# Revit family: pl-erp40160ha3_50hz
name_source: partatom
category: 機械設備
units: mm (PartAtom-declared; Revit-internal decimal feet)

## family parameters
OmniClass タイトル = Split System Air Conditioning Units
OmniClass 番号 = 23.75.10.24.21.27.27
パーツ タイプ = 標準
ロード時にボイドで切り取り = いいえ
丸型コネクタ寸法 = 直径を使用
作業面ベース = いいえ
共有 = いいえ
常に垂直 = はい
部屋計算ポイント = はい

## types (11) — shared parameters
Clearance Back = 1500  [stored 4.92126 ft]
Clearance Bottom = 1800  [stored 5.90551 ft]
Clearance Front = 1500  [stored 4.92126 ft]
Clearance Left = 1500  [stored 4.92126 ft]
Clearance Right = 1500  [stored 4.92126 ft]
Depth = 840  [stored 2.75591 ft]
IfcExportAs = IfcUnitaryEquipmentType
IfcExportType = AIRCONDITIONINGUNIT
OmniClassCode = 23-33 17 13 11
Panel Depth = 950  [stored 3.1168 ft]
Panel Height = 35  [stored 0.114829 ft]
Panel Width = 950  [stored 3.1168 ft]
URL = https://www.mitsubishielectric.co.jp
Uniclass2015Code = Pr_70_65_03_84
Uniclass2015Title = Split coil remote air cooled condensing units
Uniclass2015Version = Systems v1.9
Width = 840  [stored 2.75591 ft]
ケーブルサイズ = 0 mm
サービススペース = はい
ドレン管径 = 25 mm
ドレン管径(外径) = 32 mm
ドレン管高さ = 190
パネルマテリアル = <カテゴリ別>
仕様書バージョン = Version1.0
企業コード = 108420
冷媒ガス管高さ = 170  [stored 0.557743 ft]
冷媒液管高さ = 140  [stored 0.459318 ft]
冷媒管径 = 100 mm
分類コード = 5.0053E+13
参照している仕様書等のバージョン = 公共建築物標準仕様書（機械設備工事編）平成31年度版
吊りボルト_H = 105  [stored 0.344488 ft]
吊り位置X = 795  [stored 2.60827 ft]
吊り位置Y = 660
周波数 = 50 Hz
呼称 = 室内機_カセット形 (4方向吹出形)
始動方式 = 直入
形式 = カセット形 (4方向吹出形)
推奨ブレーカー容量 = 0 A
本体マテリアル = <カテゴリ別>
極数 = 1
法定耐用年数 = 6
消費電力 = 0 kW
消費電力_冷房 = 0 kW
消費電力_暖房 = 0 kW
発停方法 = 付属スイッチ
相 = 1
積算_科目 = 1 空気調和設備
符号 = PAC_CK4
製品出荷対象 = 国内
製品質量_パネル = 4.50 kg
製造元 = 三菱電機株式会社
設置方法 = カセット形
説明 = 店舗・事務所用パッケージエアコン(Mr.SLIM) 4方向天井カセット形
負荷分類 = 3_ファン類
運転質量 = 0.00 kg
電動機出力_送風機 = 0 kW
電圧 = 0 V
電源_H = 37
zero-valued in all types: 価格, 有効加湿量

## per-type parameters (varying)
- 天井4方向_PL-ERP40HA3: Clearance Top=265  [stored 0.869423 ft]; Height=258  [stored 0.846457 ft]; MAX風量=960.0 m³/h; MID風量=720.0 m³/h; MID風量2=660.0 m³/h; MIN風量=600.0 m³/h; 冷媒ガス管径=12.7 mm; 冷媒ガス管長さ=76.5  [stored 0.250984 ft]; 冷媒液管径=6.35 mm; 冷媒液管長さ=72.5  [stored 0.237861 ft]; 冷媒管径符号=Ac; 冷房能力=4 kW; 暖房能力=4 kW; 構成品番=PL-ERP40HA3; 製品質量=24.50 kg; 製品質量_本体=20.00 kg; 質量=29.40 kg; 音響パワーレベル(dB)=45; 音響パワーレベル_中 (dB)=44; 音響パワーレベル_弱 (dB)=43; 音響パワーレベル_強 (dB)=45; 音響パワーレベル_静 (dB)=42; 風量=960.0 m³/h; 風量_中 (㎥/min)=12; 風量_弱 (㎥/min)=11; 風量_強 (㎥/min)=16; 風量_静 (㎥/min)=10
- 天井4方向_PL-ERP45HA3: Clearance Top=265  [stored 0.869423 ft]; Height=258  [stored 0.846457 ft]; MAX風量=960.0 m³/h; MID風量=720.0 m³/h; MID風量2=660.0 m³/h; MIN風量=600.0 m³/h; 冷媒ガス管径=12.7 mm; 冷媒ガス管長さ=76.5  [stored 0.250984 ft]; 冷媒液管径=6.35 mm; 冷媒液管長さ=72.5  [stored 0.237861 ft]; 冷媒管径符号=Ac; 冷房能力=4 kW; 暖房能力=5 kW; 構成品番=PL-ERP45HA3; 製品質量=24.50 kg; 製品質量_本体=20.00 kg; 質量=29.40 kg; 音響パワーレベル(dB)=46; 音響パワーレベル_中 (dB)=44; 音響パワーレベル_弱 (dB)=43; 音響パワーレベル_強 (dB)=46; 音響パワーレベル_静 (dB)=42; 風量=960.0 m³/h; 風量_中 (㎥/min)=12; 風量_弱 (㎥/min)=11; 風量_強 (㎥/min)=16; 風量_静 (㎥/min)=10
- 天井4方向_PL-ERP50HA3: Clearance Top=265  [stored 0.869423 ft]; Height=258  [stored 0.846457 ft]; MAX風量=1080.0 m³/h; MID風量=1020.0 m³/h; MID風量2=960.0 m³/h; MIN風量=720.0 m³/h; 冷媒ガス管径=12.7 mm; 冷媒ガス管長さ=76.5  [stored 0.250984 ft]; 冷媒液管径=6.35 mm; 冷媒液管長さ=72.5  [stored 0.237861 ft]; 冷媒管径符号=Ac; 冷房能力=5 kW; 暖房能力=5 kW; 構成品番=PL-ERP50HA3; 製品質量=24.50 kg; 製品質量_本体=20.00 kg; 質量=29.40 kg; 音響パワーレベル(dB)=48; 音響パワーレベル_中 (dB)=47; 音響パワーレベル_弱 (dB)=46; 音響パワーレベル_強 (dB)=48; 音響パワーレベル_静 (dB)=44; 風量=1080.0 m³/h; 風量_中 (㎥/min)=17; 風量_弱 (㎥/min)=16; 風量_強 (㎥/min)=18; 風量_静 (㎥/min)=12
- 天井4方向_PL-ERP56HA3: Clearance Top=265  [stored 0.869423 ft]; Height=258  [stored 0.846457 ft]; MAX風量=1080.0 m³/h; MID風量=1020.0 m³/h; MID風量2=960.0 m³/h; MIN風量=720.0 m³/h; 冷媒ガス管径=12.7 mm; 冷媒ガス管長さ=76.5  [stored 0.250984 ft]; 冷媒液管径=6.35 mm; 冷媒液管長さ=72.5  [stored 0.237861 ft]; 冷媒管径符号=Ac; 冷房能力=5 kW; 暖房能力=6 kW; 構成品番=PL-ERP56HA3; 製品質量=24.50 kg; 製品質量_本体=20.00 kg; 質量=29.40 kg; 音響パワーレベル(dB)=49; 音響パワーレベル_中 (dB)=48; 音響パワーレベル_弱 (dB)=47; 音響パワーレベル_強 (dB)=49; 音響パワーレベル_静 (dB)=44; 風量=1080.0 m³/h; 風量_中 (㎥/min)=17; 風量_弱 (㎥/min)=16; 風量_強 (㎥/min)=18; 風量_静 (㎥/min)=12
- 天井4方向_PL-ERP63HA3: Clearance Top=265  [stored 0.869423 ft]; Height=258  [stored 0.846457 ft]; MAX風量=1200.0 m³/h; MID風量=1080.0 m³/h; MID風量2=960.0 m³/h; MIN風量=720.0 m³/h; 冷媒ガス管径=12.7 mm; 冷媒ガス管長さ=76.5  [stored 0.250984 ft]; 冷媒液管径=6.35 mm; 冷媒液管長さ=72.5  [stored 0.237861 ft]; 冷媒管径符号=Ac; 冷房能力=6 kW; 暖房能力=6 kW; 構成品番=PL-ERP63HA3; 製品質量=24.50 kg; 製品質量_本体=20.00 kg; 質量=29.40 kg; 音響パワーレベル(dB)=49; 音響パワーレベル_中 (dB)=48; 音響パワーレベル_弱 (dB)=47; 音響パワーレベル_強 (dB)=49; 音響パワーレベル_静 (dB)=46; 風量=1200.0 m³/h; 風量_中 (㎥/min)=18; 風量_弱 (㎥/min)=16; 風量_強 (㎥/min)=20; 風量_静 (㎥/min)=12
- 天井4方向_PL-ERP71HA3: Clearance Top=265  [stored 0.869423 ft]; Height=258  [stored 0.846457 ft]; MAX風量=1260.0 m³/h; MID風量=1140.0 m³/h; MID風量2=960.0 m³/h; MIN風量=720.0 m³/h; 冷媒ガス管径=15.88 mm; 冷媒ガス管長さ=79.5  [stored 0.260827 ft]; 冷媒液管径=9.52 mm; 冷媒液管長さ=76.5  [stored 0.250984 ft]; 冷媒管径符号=Bd; 冷房能力=6 kW; 暖房能力=7 kW; 構成品番=PL-ERP71HA3; 製品質量=24.50 kg; 製品質量_本体=20.00 kg; 質量=29.40 kg; 音響パワーレベル(dB)=51; 音響パワーレベル_中 (dB)=49; 音響パワーレベル_弱 (dB)=48; 音響パワーレベル_強 (dB)=51; 音響パワーレベル_静 (dB)=47; 風量=1260.0 m³/h; 風量_中 (㎥/min)=19; 風量_弱 (㎥/min)=16; 風量_強 (㎥/min)=21; 風量_静 (㎥/min)=12
- 天井4方向_PL-ERP80HA3: Clearance Top=265  [stored 0.869423 ft]; Height=258  [stored 0.846457 ft]; MAX風量=1380.0 m³/h; MID風量=1200.0 m³/h; MID風量2=1080.0 m³/h; MIN風量=960.0 m³/h; 冷媒ガス管径=15.88 mm; 冷媒ガス管長さ=79.5  [stored 0.260827 ft]; 冷媒液管径=9.52 mm; 冷媒液管長さ=76.5  [stored 0.250984 ft]; 冷媒管径符号=Bd; 冷房能力=7 kW; 暖房能力=8 kW; 構成品番=PL-ERP80HA3; 製品質量=24.50 kg; 製品質量_本体=20.00 kg; 質量=29.40 kg; 音響パワーレベル(dB)=52; 音響パワーレベル_中 (dB)=51; 音響パワーレベル_弱 (dB)=50; 音響パワーレベル_強 (dB)=52; 音響パワーレベル_静 (dB)=49; 風量=1380.0 m³/h; 風量_中 (㎥/min)=20; 風量_弱 (㎥/min)=18; 風量_強 (㎥/min)=23; 風量_静 (㎥/min)=16
- 天井4方向_PL-ERP112HA3: Clearance Top=305  [stored 1.00066 ft]; Height=298  [stored 0.97769 ft]; MAX風量=2100.0 m³/h; MID風量=1800.0 m³/h; MID風量2=1440.0 m³/h; MIN風量=1200.0 m³/h; 冷媒ガス管径=15.88 mm; 冷媒ガス管長さ=79.5  [stored 0.260827 ft]; 冷媒液管径=9.52 mm; 冷媒液管長さ=76.5  [stored 0.250984 ft]; 冷媒管径符号=Bd; 冷房能力=10 kW; 暖房能力=11 kW; 構成品番=PL-ERP112HA3; 製品質量=29.50 kg; 製品質量_本体=25.00 kg; 質量=35.40 kg; 音響パワーレベル(dB)=59; 音響パワーレベル_中 (dB)=56; 音響パワーレベル_弱 (dB)=53; 音響パワーレベル_強 (dB)=59; 音響パワーレベル_静 (dB)=51; 風量=2100.0 m³/h; 風量_中 (㎥/min)=30; 風量_弱 (㎥/min)=24; 風量_強 (㎥/min)=35; 風量_静 (㎥/min)=20
- 天井4方向_PL-ERP140HA3: Clearance Top=305  [stored 1.00066 ft]; Height=298  [stored 0.97769 ft]; MAX風量=2280.0 m³/h; MID風量=1860.0 m³/h; MID風量2=1560.0 m³/h; MIN風量=1320.0 m³/h; 冷媒ガス管径=15.88 mm; 冷媒ガス管長さ=79.5  [stored 0.260827 ft]; 冷媒液管径=9.52 mm; 冷媒液管長さ=76.5  [stored 0.250984 ft]; 冷媒管径符号=Bd; 冷房能力=13 kW; 暖房能力=14 kW; 構成品番=PL-ERP140HA3; 製品質量=29.50 kg; 製品質量_本体=25.00 kg; 質量=35.40 kg; 音響パワーレベル(dB)=62; 音響パワーレベル_中 (dB)=60; 音響パワーレベル_弱 (dB)=55; 音響パワーレベル_強 (dB)=62; 音響パワーレベル_静 (dB)=53; 風量=2280.0 m³/h; 風量_中 (㎥/min)=31; 風量_弱 (㎥/min)=26; 風量_強 (㎥/min)=38; 風量_静 (㎥/min)=22
- 天井4方向_PL-ERP160HA3: Clearance Top=305  [stored 1.00066 ft]; Height=298  [stored 0.97769 ft]; MAX風量=2280.0 m³/h; MID風量=1860.0 m³/h; MID風量2=1680.0 m³/h; MIN風量=1500.0 m³/h; 冷媒ガス管径=15.88 mm; 冷媒ガス管長さ=79.5  [stored 0.260827 ft]; 冷媒液管径=9.52 mm; 冷媒液管長さ=76.5  [stored 0.250984 ft]; 冷媒管径符号=Bd; 冷房能力=14 kW; 暖房能力=16 kW; 構成品番=PL-ERP160HA3; 製品質量=29.50 kg; 製品質量_本体=25.00 kg; 質量=35.40 kg; 音響パワーレベル(dB)=62; 音響パワーレベル_中 (dB)=60; 音響パワーレベル_弱 (dB)=57; 音響パワーレベル_強 (dB)=62; 音響パワーレベル_静 (dB)=56; 風量=2280.0 m³/h; 風量_中 (㎥/min)=31; 風量_弱 (㎥/min)=28; 風量_強 (㎥/min)=38; 風量_静 (㎥/min)=25
- 天井4方向_PL-HRP80HA3: Clearance Top=305  [stored 1.00066 ft]; Height=298  [stored 0.97769 ft]; MAX風量=1380.0 m³/h; MID風量=1200.0 m³/h; MID風量2=1020.0 m³/h; MIN風量=900.0 m³/h; 冷媒ガス管径=15.88 mm; 冷媒ガス管長さ=79.5  [stored 0.260827 ft]; 冷媒液管径=9.52 mm; 冷媒液管長さ=76.5  [stored 0.250984 ft]; 冷媒管径符号=Bd; 冷房能力=7 kW; 暖房能力=8 kW; 構成品番=PL-HRP80HA3; 製品質量=30.50 kg; 製品質量_本体=26.00 kg; 質量=36.60 kg; 音響パワーレベル(dB)=52; 音響パワーレベル_中 (dB)=50; 音響パワーレベル_弱 (dB)=48; 音響パワーレベル_強 (dB)=52; 音響パワーレベル_静 (dB)=46; 風量=1380.0 m³/h; 風量_中 (㎥/min)=20; 風量_弱 (㎥/min)=17; 風量_強 (㎥/min)=23; 風量_静 (㎥/min)=15

note: [stored X ft] marks values corroborated as IEEE doubles in the binary element streams (Revit-internal decimal feet)

## geometry (parser evidence)
native form markers: Blend x16
no freeform markers — native parametric forms only
